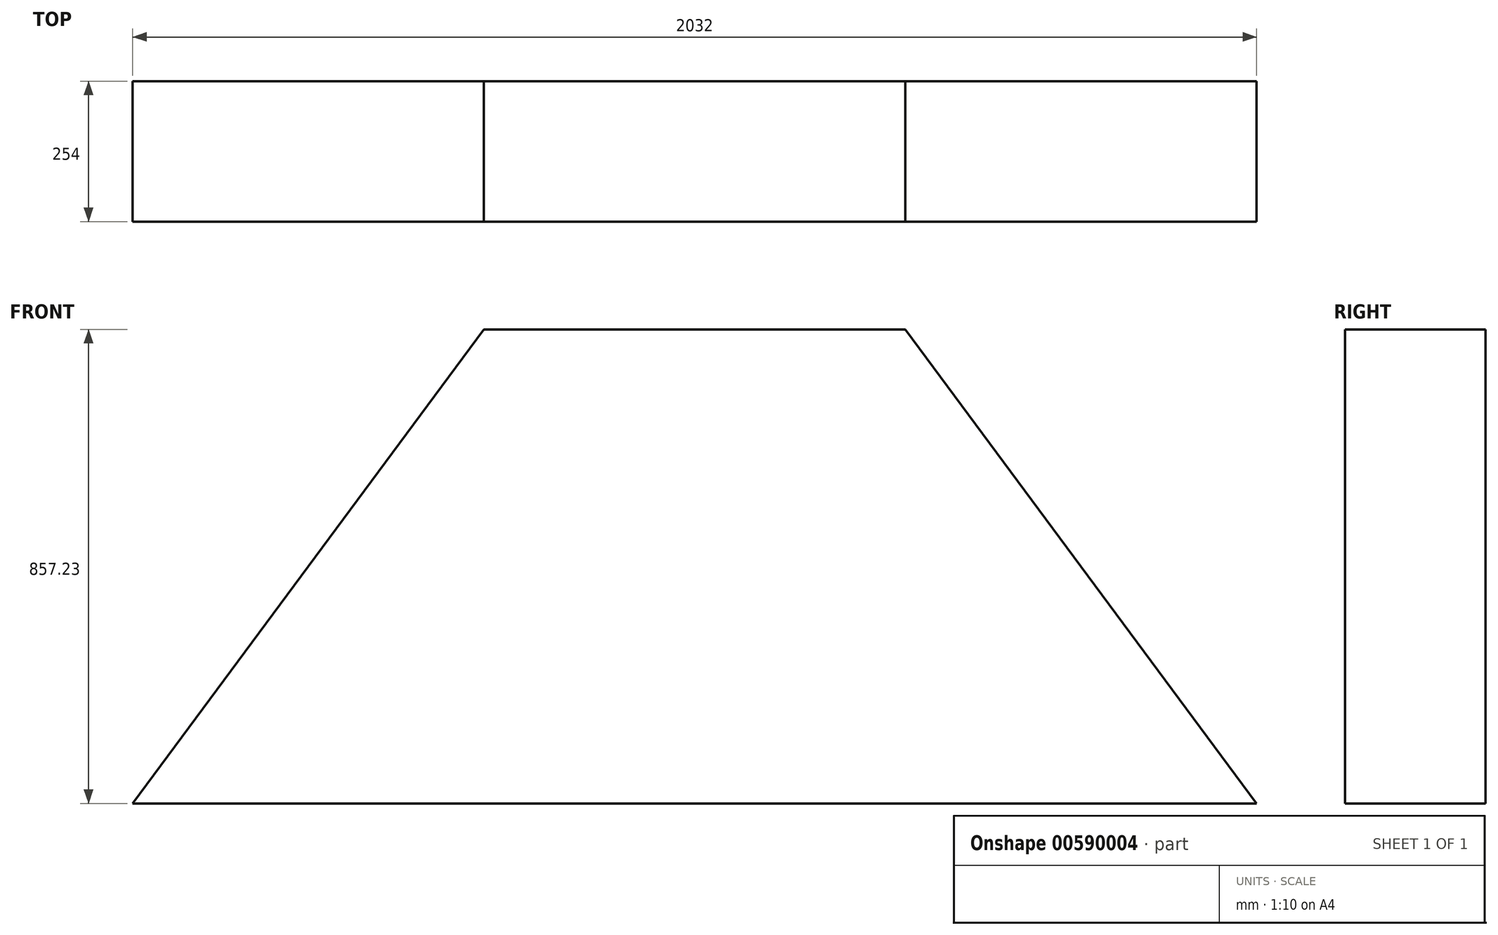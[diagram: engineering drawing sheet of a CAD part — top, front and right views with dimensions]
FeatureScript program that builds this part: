
annotation { "Feature Type Name" : "Feature", "Feature Type Description" : "" }
export const myFeature = defineFeature(function(context is Context, id is Id, definition is map)
    precondition{}
    {
        {
            var Q0;
            Q0=qCreatedBy(makeId("Front.planeOp"),FACE);
            var sketch = newSketch(context, id + "F0", { "sketchPlane" : qUnion([Q0])});
            skLineSegment(sketch, "E0", {"start": v(0, 0) * mm, "end": v(635, 857.23) * mm});
            skLineSegment(sketch, "E1", {"start": v(635, 857.23) * mm, "end": v(1397, 857.23) * mm});
            skLineSegment(sketch, "E2", {"start": v(1397, 857.23) * mm, "end": v(2032, 0) * mm});
            skLineSegment(sketch, "E3", {"start": v(2032, 0) * mm, "end": v(0, 0) * mm});
            skSolve(sketch);
        }
        {
            var Q0;
            Q0 = qSketchRegion(id + "F0", true);
            var Q1;
            Q1=makeQuery(id+"F0.imprint","IMPRINT",FACE,{"disambiguationData":[TD([[makeQuery(id+"F0.imprint","IMPRINT",EDGE,{"derivedFrom":sQuery(id+"F0.wireOp",EDGE,"E0")}),-1.0]])]});
            extrude(context, id + "F1", {"entities" : qUnion([Q0, Q1]), "depth" : 254 * mm, "offsetDistance" : 25.4 * mm});
        }
    });
